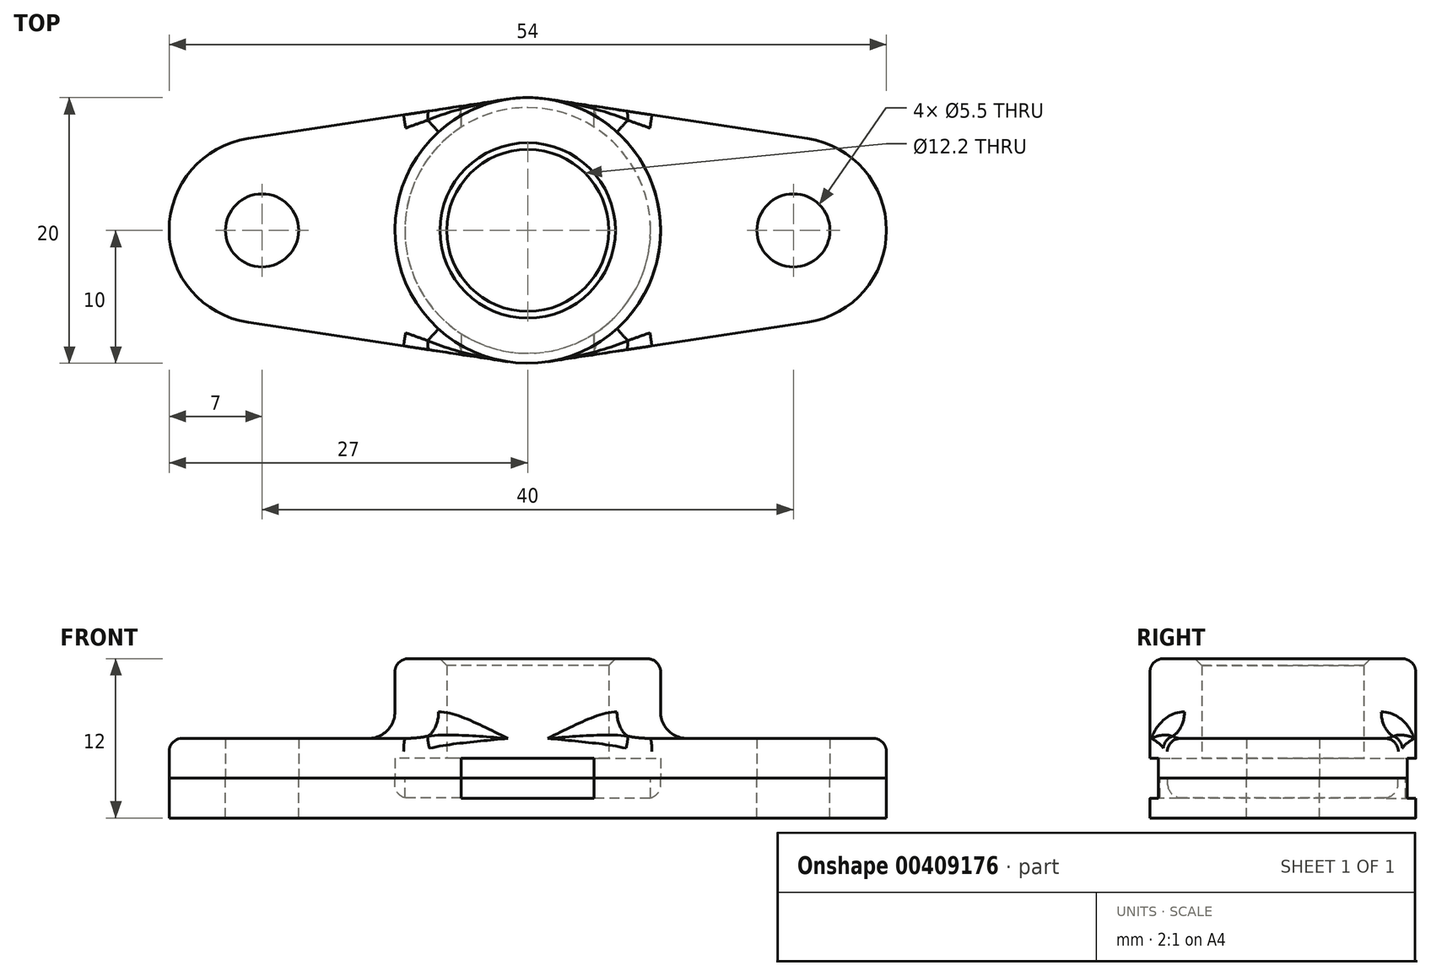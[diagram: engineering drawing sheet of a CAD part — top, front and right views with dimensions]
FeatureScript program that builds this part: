
annotation { "Feature Type Name" : "Feature", "Feature Type Description" : "" }
export const myFeature = defineFeature(function(context is Context, id is Id, definition is map)
    precondition{}
    {
        {
            var Q0;
            Q0=qCreatedBy(makeId("Top.planeOp"),FACE);
            var sketch = newSketch(context, id + "F0", { "sketchPlane" : qUnion([Q0])});
            skCircle(sketch, "E0", {"center": v(0, 0) * mm, "radius": 10 * mm});
            skCircle(sketch, "E1", {"center": v(0, 0) * mm, "radius": 6.1 * mm});
            skCircle(sketch, "E2", {"center": v(0, 0) * mm, "radius": 5 * mm});
            skCircle(sketch, "E3", {"center": v(0, 0) * mm, "radius": 9.25 * mm});
            skLineSegment(sketch, "E4", {"start": v(-5, -8.66) * mm, "end": v(-5, -9.36) * mm});
            skCircle(sketch, "E5", {"center": v(-20, 0) * mm, "radius": 2.75 * mm});
            skArc(sketch, "E6", {"start": v(-21.05, 6.92) * mm, "mid": v(-27, 0) * mm, "end": v(-21.05, -6.92) * mm});
            skLineSegment(sketch, "E7", {"start": v(-21.05, 6.92) * mm, "end": v(-1.5, 9.89) * mm});
            skLineSegment(sketch, "E8", {"start": v(-21.05, -6.92) * mm, "end": v(-1.5, -9.89) * mm});
            skLineSegment(sketch, "E9.MirrorCS", {"start": v(-5, 8.66) * mm, "end": v(-5, 9.36) * mm});
            skLineSegment(sketch, "E10.MirrorCS", {"start": v(21.05, 6.92) * mm, "end": v(1.5, 9.89) * mm});
            skLineSegment(sketch, "E11.MirrorCS", {"start": v(5, 8.66) * mm, "end": v(5, 9.36) * mm});
            skArc(sketch, "E12.MirrorCS", {"start": v(21.05, 6.92) * mm, "mid": v(27, 0) * mm, "end": v(21.05, -6.92) * mm});
            skCircle(sketch, "E13.MirrorC", {"center": v(20, 0) * mm, "radius": 2.75 * mm});
            skLineSegment(sketch, "E14.MirrorCS", {"start": v(21.05, -6.92) * mm, "end": v(1.5, -9.89) * mm});
            skLineSegment(sketch, "E15.MirrorCS", {"start": v(5, -8.66) * mm, "end": v(5, -9.36) * mm});
            skSolve(sketch);
        }
        {
            var Q0;
            {var subQ0=sQuery(id+"F0.wireOp",EDGE,"E4");Q0=makeQuery(id+"F0.imprint","IMPRINT",FACE,{"disambiguationData":[TD([[makeQuery(id+"F0.imprint","IMPRINT",EDGE,{"derivedFrom":subQ0}),1.0]])]});}
            var Q1;
            Q1=makeQuery(id+"F0.imprint","IMPRINT",FACE,{"disambiguationData":[TD([[makeQuery(id+"F0.imprint","IMPRINT",EDGE,{"derivedFrom":sQuery(id+"F0.wireOp",EDGE,"E3")}),-1.0]])]});
            var Q2;
            {var subQ3=sQuery(id+"F0.wireOp",EDGE,"E11.MirrorCS");Q2=makeQuery(id+"F0.imprint","IMPRINT",FACE,{"disambiguationData":[TD([[makeQuery(id+"F0.imprint","IMPRINT",EDGE,{"derivedFrom":subQ3}),1.0]])]});}
            var Q3;
            {var subQ0=sQuery(id+"F0.wireOp",EDGE,"E4");Q3=makeQuery(id+"F0.imprint","IMPRINT",FACE,{"disambiguationData":[TD([[makeQuery(id+"F0.imprint","IMPRINT",EDGE,{"derivedFrom":subQ0}),-1.0]])]});}
            var Q4;
            Q4=makeQuery(id+"F0.imprint","IMPRINT",FACE,{"disambiguationData":[TD([[makeQuery(id+"F0.imprint","IMPRINT",EDGE,{"derivedFrom":sQuery(id+"F0.wireOp",EDGE,"E1")}),-1.0]])]});
            var Q5;
            {var subQ3=sQuery(id+"F0.wireOp",EDGE,"E9.MirrorCS");Q5=makeQuery(id+"F0.imprint","IMPRINT",FACE,{"disambiguationData":[TD([[makeQuery(id+"F0.imprint","IMPRINT",EDGE,{"derivedFrom":subQ3}),-1.0]])]});}
            var Q6;
            {var subQ3=sQuery(id+"F0.wireOp",EDGE,"E15.MirrorCS");Q6=makeQuery(id+"F0.imprint","IMPRINT",FACE,{"disambiguationData":[TD([[makeQuery(id+"F0.imprint","IMPRINT",EDGE,{"derivedFrom":subQ3}),-1.0]])]});}
            var Q7;
            {var subQ0=sQuery(id+"F0.wireOp",EDGE,"E11.MirrorCS");Q7=makeQuery(id+"F0.imprint","IMPRINT",FACE,{"disambiguationData":[TD([[makeQuery(id+"F0.imprint","IMPRINT",EDGE,{"derivedFrom":subQ0}),-1.0]])]});}
            extrude(context, id + "F1", {"entities" : qUnion([Q0, Q1, Q2, Q3, Q4, Q5, Q6, Q7]), "depth" : 3 * mm, "offsetDistance" : 25 * mm});
        }
        {
            var Q0;
            Q0=makeQuery(id+"F0.imprint","IMPRINT",FACE,{"disambiguationData":[TD([[makeQuery(id+"F0.imprint","IMPRINT",EDGE,{"derivedFrom":sQuery(id+"F0.wireOp",EDGE,"E0")}),1.0]])]});
            var Q1;
            Q1=makeQuery(id+"F0.imprint","IMPRINT",FACE,{"disambiguationData":[TD([[makeQuery(id+"F0.imprint","IMPRINT",EDGE,{"derivedFrom":sQuery(id+"F0.wireOp",EDGE,"E1")}),-1.0]])]});
            extrude(context, id + "F2", {"entities" : qUnion([Q0, Q1]), "operationType" : NewBodyOperationType.ADD, "depth" : 9 * mm, "offsetDistance" : 25 * mm});
        }
        {
            var Q0;
            Q0=makeQuery(id+"F0.imprint","IMPRINT",FACE,{"disambiguationData":[TD([[makeQuery(id+"F0.imprint","IMPRINT",EDGE,{"derivedFrom":sQuery(id+"F0.wireOp",EDGE,"E1")}),-1.0]])]});
            var Q1;
            {var subQ0=sQuery(id+"F0.wireOp",EDGE,"5FznAjd5-Rlev-DzMA-E21E-VBbVsZXluKNu");Q1=makeQuery(id+"F0.imprint","IMPRINT",FACE,{"disambiguationData":[TD([[makeQuery(id+"F0.imprint","IMPRINT",EDGE,{"derivedFrom":subQ0}),1.0]])]});}
            var Q2;
            Q2=makeQuery(id+"F0.imprint","IMPRINT",FACE,{"disambiguationData":[TD([[makeQuery(id+"F0.imprint","IMPRINT",EDGE,{"derivedFrom":sQuery(id+"F0.wireOp",EDGE,"E3")}),-1.0]])]});
            var Q3;
            {var subQ3=sQuery(id+"F0.wireOp",EDGE,"E9.MirrorCS");Q3=makeQuery(id+"F0.imprint","IMPRINT",FACE,{"disambiguationData":[TD([[makeQuery(id+"F0.imprint","IMPRINT",EDGE,{"derivedFrom":subQ3}),-1.0]])]});}
            var Q4;
            {var subQ3=sQuery(id+"F0.wireOp",EDGE,"E11.MirrorCS");Q4=makeQuery(id+"F0.imprint","IMPRINT",FACE,{"disambiguationData":[TD([[makeQuery(id+"F0.imprint","IMPRINT",EDGE,{"derivedFrom":subQ3}),1.0]])]});}
            var Q5;
            {var subQ3=sQuery(id+"F0.wireOp",EDGE,"E15.MirrorCS");Q5=makeQuery(id+"F0.imprint","IMPRINT",FACE,{"disambiguationData":[TD([[makeQuery(id+"F0.imprint","IMPRINT",EDGE,{"derivedFrom":subQ3}),-1.0]])]});}
            var Q6;
            {var subQ0=sQuery(id+"F0.wireOp",EDGE,"E4");Q6=makeQuery(id+"F0.imprint","IMPRINT",FACE,{"disambiguationData":[TD([[makeQuery(id+"F0.imprint","IMPRINT",EDGE,{"derivedFrom":subQ0}),1.0]])]});}
            extrude(context, id + "F3", {"entities" : qUnion([Q0, Q1, Q2, Q3, Q4, Q5, Q6]), "operationType" : NewBodyOperationType.REMOVE, "depth" : 1.5 * mm, "offsetDistance" : 25 * mm});
        }
        {
            var Q0;
            Q0=makeQuery(id+"F2.boolean.opBoolean","INTERSECT",EDGE,{"derivedFrom":[makeQuery(id+"F1.opExtrude","CAP_FACE",FACE,{"disambiguationData":[OSD([sQuery(id+"F0.wireOp",EDGE,"CR5xfrm7-slQB-9y9x-49ej-DvTKbvRHMWAN"),sQuery(id+"F0.wireOp",EDGE,"E1"),sQuery(id+"F0.wireOp",EDGE,"M7DjQCVk-RdmV-3Hag-MnrL-rbCDdXIXaqB2"),sQuery(id+"F0.wireOp",EDGE,"RkNN1qvF-Dhff-J5sZ-8Obf-itKSpEIQRsD5"),sQuery(id+"F0.wireOp",EDGE,"vTTUK6wD-1rki-MkEa-Snrt-uhQ54I2DBWBJ"),sQuery(id+"F0.wireOp",EDGE,"aeZG0UcR-o17r-frF0-7Pf3-XlpCiled6ced"),sQuery(id+"F0.wireOp",EDGE,"caf4d550-849c-44d5-98c3-947d7a4541f20.MirrorC"),sQuery(id+"F0.wireOp",EDGE,"9f394b66-eea1-4626-9a4b-a5357dff60b50.MirrorCS"),sQuery(id+"F0.wireOp",EDGE,"Hp2xihsS-EqJb-Bp0g-DRQg-preZB8XAk3cP")])],"isStart":false}),makeQuery(id+"F2.opExtrude","SWEPT_FACE",FACE,{"disambiguationData":[OSD([sQuery(id+"F0.wireOp",EDGE,"E0")])]})]});
            fillet(context, id + "F4", {"entities" : qUnion([Q0]), "radius" : 2 * mm, "tangentPropagation" : true, "allowEdgeOverflow" : false});
        }
        {
            var Q0;
            Q0=makeQuery(id+"F2.opExtrude","CAP_EDGE",EDGE,{"disambiguationData":[OSD([sQuery(id+"F0.wireOp",EDGE,"E1")])],"isStart":false});
            var Q1;
            Q1=makeQuery(id+"F1.opExtrude","CAP_EDGE",EDGE,{"disambiguationData":[OSD([sQuery(id+"F0.wireOp",EDGE,"CR5xfrm7-slQB-9y9x-49ej-DvTKbvRHMWAN")])],"isStart":false});
            var Q2;
            Q2=makeQuery(id+"F1.opExtrude","CAP_EDGE",EDGE,{"disambiguationData":[OSD([sQuery(id+"F0.wireOp",EDGE,"M7DjQCVk-RdmV-3Hag-MnrL-rbCDdXIXaqB2")])],"isStart":false});
            chamfer(context, id + "F5", {"entities" : qUnion([Q0, Q1, Q2]), "width" : 0.5 * mm, "tangentPropagation" : true});
        }
        {
            var Q0;
            {var subQ0=sQuery(id+"F0.wireOp",EDGE,"E4");Q0=makeQuery(id+"F0.imprint","IMPRINT",FACE,{"disambiguationData":[TD([[makeQuery(id+"F0.imprint","IMPRINT",EDGE,{"derivedFrom":subQ0}),-1.0]])]});}
            var Q1;
            {var subQ0=sQuery(id+"F0.wireOp",EDGE,"E11.MirrorCS");Q1=makeQuery(id+"F0.imprint","IMPRINT",FACE,{"disambiguationData":[TD([[makeQuery(id+"F0.imprint","IMPRINT",EDGE,{"derivedFrom":subQ0}),-1.0]])]});}
            var Q2;
            Q2=makeQuery(id+"F0.imprint","IMPRINT",FACE,{"disambiguationData":[TD([[makeQuery(id+"F0.imprint","IMPRINT",EDGE,{"derivedFrom":sQuery(id+"F0.wireOp",EDGE,"E1")}),-1.0]])]});
            var Q3;
            Q3=makeQuery(id+"F0.imprint","IMPRINT",FACE,{"disambiguationData":[TD([[makeQuery(id+"F0.imprint","IMPRINT",EDGE,{"derivedFrom":sQuery(id+"F0.wireOp",EDGE,"E2")}),1.0]])]});
            var Q4;
            Q4=makeQuery(id+"F0.imprint","IMPRINT",FACE,{"disambiguationData":[TD([[makeQuery(id+"F0.imprint","IMPRINT",EDGE,{"derivedFrom":sQuery(id+"F0.wireOp",EDGE,"E1")}),1.0]])]});
            var Q5;
            Q5=makeQuery(id+"F0.imprint","IMPRINT",FACE,{"disambiguationData":[TD([[makeQuery(id+"F0.imprint","IMPRINT",EDGE,{"derivedFrom":sQuery(id+"F0.wireOp",EDGE,"E3")}),-1.0]])]});
            var Q6;
            {var subQ3=sQuery(id+"F0.wireOp",EDGE,"E11.MirrorCS");Q6=makeQuery(id+"F0.imprint","IMPRINT",FACE,{"disambiguationData":[TD([[makeQuery(id+"F0.imprint","IMPRINT",EDGE,{"derivedFrom":subQ3}),1.0]])]});}
            var Q7;
            {var subQ3=sQuery(id+"F0.wireOp",EDGE,"E9.MirrorCS");Q7=makeQuery(id+"F0.imprint","IMPRINT",FACE,{"disambiguationData":[TD([[makeQuery(id+"F0.imprint","IMPRINT",EDGE,{"derivedFrom":subQ3}),-1.0]])]});}
            var Q8;
            {var subQ0=sQuery(id+"F0.wireOp",EDGE,"E4");Q8=makeQuery(id+"F0.imprint","IMPRINT",FACE,{"disambiguationData":[TD([[makeQuery(id+"F0.imprint","IMPRINT",EDGE,{"derivedFrom":subQ0}),1.0]])]});}
            var Q9;
            {var subQ3=sQuery(id+"F0.wireOp",EDGE,"E15.MirrorCS");Q9=makeQuery(id+"F0.imprint","IMPRINT",FACE,{"disambiguationData":[TD([[makeQuery(id+"F0.imprint","IMPRINT",EDGE,{"derivedFrom":subQ3}),-1.0]])]});}
            extrude(context, id + "F6", {"entities" : qUnion([Q0, Q1, Q2, Q3, Q4, Q5, Q6, Q7, Q8, Q9]), "oppositeDirection" : true, "depth" : 3 * mm, "offsetDistance" : 25 * mm});
        }
        {
            var Q0;
            {var subQ0=sQuery(id+"F0.wireOp",EDGE,"5FznAjd5-Rlev-DzMA-E21E-VBbVsZXluKNu");Q0=makeQuery(id+"F0.imprint","IMPRINT",FACE,{"disambiguationData":[TD([[makeQuery(id+"F0.imprint","IMPRINT",EDGE,{"derivedFrom":subQ0}),1.0]])]});}
            var Q1;
            Q1=makeQuery(id+"F0.imprint","IMPRINT",FACE,{"disambiguationData":[TD([[makeQuery(id+"F0.imprint","IMPRINT",EDGE,{"derivedFrom":sQuery(id+"F0.wireOp",EDGE,"E3")}),-1.0]])]});
            var Q2;
            {var subQ0=sQuery(id+"F0.wireOp",EDGE,"E4");Q2=makeQuery(id+"F0.imprint","IMPRINT",FACE,{"disambiguationData":[TD([[makeQuery(id+"F0.imprint","IMPRINT",EDGE,{"derivedFrom":subQ0}),1.0]])]});}
            var Q3;
            {var subQ3=sQuery(id+"F0.wireOp",EDGE,"E15.MirrorCS");Q3=makeQuery(id+"F0.imprint","IMPRINT",FACE,{"disambiguationData":[TD([[makeQuery(id+"F0.imprint","IMPRINT",EDGE,{"derivedFrom":subQ3}),-1.0]])]});}
            var Q4;
            {var subQ3=sQuery(id+"F0.wireOp",EDGE,"E9.MirrorCS");Q4=makeQuery(id+"F0.imprint","IMPRINT",FACE,{"disambiguationData":[TD([[makeQuery(id+"F0.imprint","IMPRINT",EDGE,{"derivedFrom":subQ3}),-1.0]])]});}
            var Q5;
            {var subQ3=sQuery(id+"F0.wireOp",EDGE,"E11.MirrorCS");Q5=makeQuery(id+"F0.imprint","IMPRINT",FACE,{"disambiguationData":[TD([[makeQuery(id+"F0.imprint","IMPRINT",EDGE,{"derivedFrom":subQ3}),1.0]])]});}
            extrude(context, id + "F7", {"entities" : qUnion([Q0, Q1, Q2, Q3, Q4, Q5]), "operationType" : NewBodyOperationType.REMOVE, "oppositeDirection" : true, "depth" : 1.5 * mm, "offsetDistance" : 25 * mm});
        }
        {
            var Q0;
            Q0=makeQuery(id+"F1.opExtrude","CAP_EDGE",EDGE,{"disambiguationData":[OSD([sQuery(id+"F0.wireOp",EDGE,"RkNN1qvF-Dhff-J5sZ-8Obf-itKSpEIQRsD5")])],"isStart":false});
            var Q1;
            Q1=makeQuery(id+"F3.boolean.opBoolean","COPY",EDGE,{"derivedFrom":makeQuery(id+"F3.opExtrude","SWEPT_EDGE",EDGE,{"disambiguationData":[OSD([sQuery(id+"F0.wireOp",EDGE,"Hp2xihsS-EqJb-Bp0g-DRQg-preZB8XAk3cP"),sQuery(id+"F0.wireOp",EDGE,"5FznAjd5-Rlev-DzMA-E21E-VBbVsZXluKNu")])]})});
            var Q2;
            Q2=makeQuery(id+"F3.boolean.opBoolean","COPY",EDGE,{"derivedFrom":makeQuery(id+"F3.opExtrude","SWEPT_EDGE",EDGE,{"disambiguationData":[OSD([sQuery(id+"F0.wireOp",EDGE,"E0"),sQuery(id+"F0.wireOp",EDGE,"5FznAjd5-Rlev-DzMA-E21E-VBbVsZXluKNu")])]})});
            var Q3;
            Q3=makeQuery(id+"F3.boolean.opBoolean","COPY",EDGE,{"derivedFrom":makeQuery(id+"F3.opExtrude","SWEPT_EDGE",EDGE,{"disambiguationData":[OSD([sQuery(id+"F0.wireOp",EDGE,"Hp2xihsS-EqJb-Bp0g-DRQg-preZB8XAk3cP"),sQuery(id+"F0.wireOp",EDGE,"b79474f3-426c-4147-9d2d-4efb16d03d300.MirrorCS")])]})});
            var Q4;
            Q4=makeQuery(id+"F3.boolean.opBoolean","COPY",EDGE,{"derivedFrom":makeQuery(id+"F3.opExtrude","SWEPT_EDGE",EDGE,{"disambiguationData":[OSD([sQuery(id+"F0.wireOp",EDGE,"E0"),sQuery(id+"F0.wireOp",EDGE,"b79474f3-426c-4147-9d2d-4efb16d03d300.MirrorCS")])]})});
            var Q5;
            Q5=makeQuery(id+"F2.opExtrude","CAP_EDGE",EDGE,{"disambiguationData":[OSD([sQuery(id+"F0.wireOp",EDGE,"E0")])],"isStart":false});
            var Q6;
            {var subQ0=sQuery(id+"F0.wireOp",EDGE,"E0");Q6=makeQuery(id+"F7.boolean.opBoolean","COPY",EDGE,{"derivedFrom":makeQuery(id+"F7.opExtrude","CAP_EDGE",EDGE,{"disambiguationData":[OSD([subQ0]),TDD([makeQuery(id+"F0.imprint","IMPRINT",EDGE,{"disambiguationData":[TD([[makeQuery(id+"F0.imprint","INTERSECT",VERTEX,{"derivedFrom":[subQ0,sQuery(id+"F0.wireOp",EDGE,"E4")]}),1.0]])],"derivedFrom":subQ0})])],"isStart":false})});}
            var Q7;
            {var subQ0=sQuery(id+"F0.wireOp",EDGE,"E0");Q7=makeQuery(id+"F7.boolean.opBoolean","COPY",EDGE,{"derivedFrom":makeQuery(id+"F7.opExtrude","CAP_EDGE",EDGE,{"disambiguationData":[OSD([subQ0]),TDD([makeQuery(id+"F0.imprint","IMPRINT",EDGE,{"disambiguationData":[TD([[makeQuery(id+"F0.imprint","INTERSECT",VERTEX,{"derivedFrom":[subQ0,sQuery(id+"F0.wireOp",EDGE,"E11.MirrorCS")]}),1.0]])],"derivedFrom":subQ0})])],"isStart":false})});}
            var Q8;
            Q8=makeQuery(id+"F1.opExtrude","CAP_EDGE",EDGE,{"disambiguationData":[OSD([sQuery(id+"F0.wireOp",EDGE,"E12.MirrorCS")])],"isStart":false});
            var Q9;
            Q9=makeQuery(id+"F1.opExtrude","CAP_EDGE",EDGE,{"disambiguationData":[OSD([sQuery(id+"F0.wireOp",EDGE,"E6")])],"isStart":false});
            fillet(context, id + "F8", {"entities" : qUnion([Q0, Q1, Q2, Q3, Q4, Q5, Q6, Q7, Q8, Q9]), "radius" : 1 * mm, "tangentPropagation" : true, "allowEdgeOverflow" : false});
        }
    });
